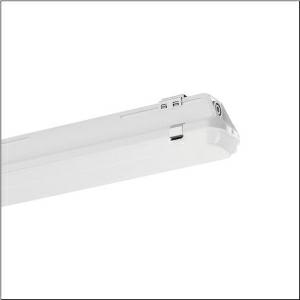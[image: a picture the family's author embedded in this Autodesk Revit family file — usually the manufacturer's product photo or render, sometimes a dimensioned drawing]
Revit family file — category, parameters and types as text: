
# Revit family: monsun_11_parking_51fg20dp440l
name_source: partatom
category: Lighting Fixtures
units: mm (PartAtom-declared; Revit-internal decimal feet)

## family parameters
Cut with Voids When Loaded = No
Host = Face
Light Source = No
Part Type = Normal
Room Calculation Point = No
Round Connector Dimension = Use Diameter
Shared = No

## types (1)
- --- (1 x LED, 4840 lm, 28.1 W, 4000K)
    Apparent Load = 28 VA
    CIE Flux Codes = 45 75 93 94 100
    Color Rendering = 80
    Color Temperature = 4000K
    Default Elevation = 1800 mm
    Description = Monsun 11 parking, damp-proof luminaire, chain hanger, primary optical cover: enclosure, of PC, light emission: direct distribution, primary light characteristic: symmetric, installation type: suspended mounting, surface-mounted, horizontal mounting, vertical mounting, LED, rated luminous flux: 4.840lm, luminous efficacy: 172lm/W, light colour: 840, colour temperature: 4000K, control gear: DALI 2, with terminal, 5-pole, max. 2.5mm², mains connection: 220..240V, AC, 50/60Hz, rated input power: 28W, housing, of glass-fibre reinforced polyester, uncoated, bright grey, incl. chain hanger, length: 1.590mm, width: 90mm, height: 88mm, clip for enclosure, of stainless steel (V2A), ceiling mounting element, of stainless steel (V2A), chain hanger, of stainless steel (V2A), protection rating (complete): IP66, insulation class (complete): insulation class I (protective earthing), certification: CE, ENEC, VDE, UKCA, protection symbol: D, impact resistance: IK08, permissible operating ambient temperature: -25..+40°C, standard: EN 50419, EN 60598-2-1, corresponds to IFS (International Featured Standards) requirements for safety and quality in the food industry, for indoor or canopied outdoor use, no direct snow, no direct sun, no direct rain, LABS conformity tested according to VDMA 24364:2018-05, contact your sales advisor before using the luminaires in applications with unclear chemical exposure, large temperature fluctuations or condensation-forming humidity, packaging unit: 1 piece
    Height = 89 mm
    Lamp = 1 x LED
    Lamp Light Flux = 4840 lm
    Lamp Power = 28.1 W
    Lamp count = 1
    Length = 1590 mm
    Luminous efficacy = 172 lm/W
    Manufacturer = Siteco
    ModVariant = No
    Model = 51FG20DP440L
    Mounting Place = Ceiling
    Mounting Type = Surface mounted
    Number of Poles = 1
    OnlyDefault = Yes
    Power Factor = 1
    Product Name = Monsun 11 parking
    Product group = damp-proof luminaire
    ProductGroupID = 300
    Protection Class = Protection class I
    Protection Degree = IP 66
    RLX_Detail_Level = 1
    RLX_Emergency_Light_Flux = 0 lm
    RLX_Emergency_Type = 0
    RLX_Emergency_Type_DB = No
    RlxData = <blob elided: 92337 chars, md5=2177090f>
    Socket = socket
    Standby Power = 0 W
    System Light Flux = 4840 lm
    System Power = 28 W
    Type Comments = factory setting: luminous flux: 100 % | dim-lin: 254 | 193 mA
    Type Image = l_1349237.jpg
    URL = http://relux.com
    VarID = @adj_033555
    Voltage = 0 V
    Weight = 0.00 kg
    Width = 90 mm

## geometry (parser evidence)
native form markers: Blend x4, Sweep x15
no freeform markers — native parametric forms only
